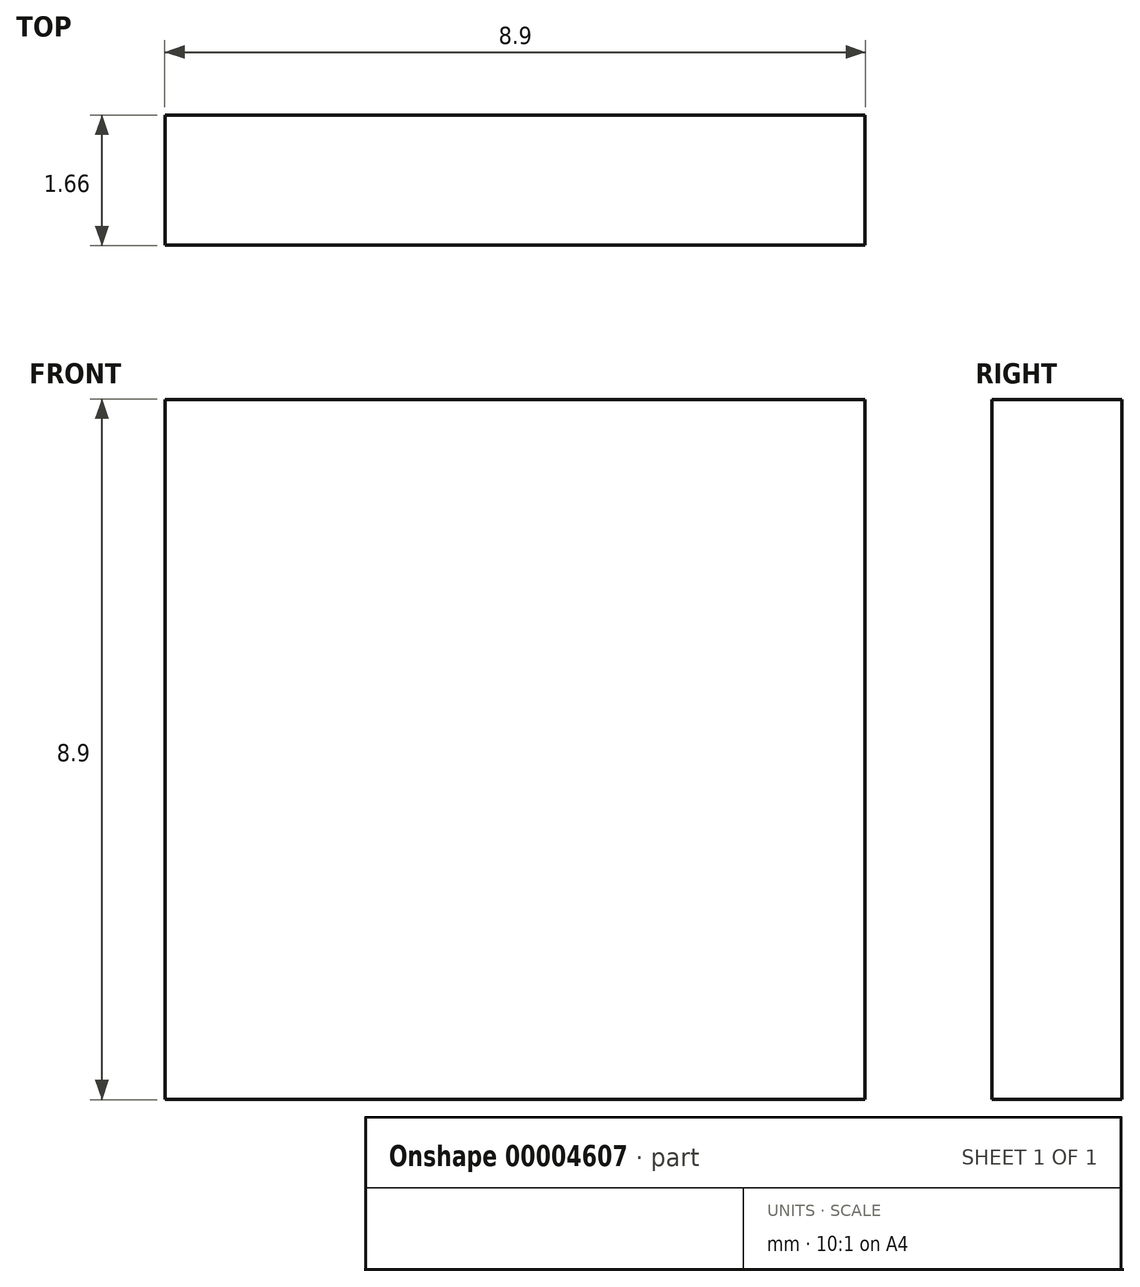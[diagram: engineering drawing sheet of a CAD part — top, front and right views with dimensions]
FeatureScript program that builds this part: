
annotation { "Feature Type Name" : "Feature", "Feature Type Description" : "" }
export const myFeature = defineFeature(function(context is Context, id is Id, definition is map)
    precondition{}
    {
        {
            var Q0;
            Q0=qCreatedBy(makeId("Right.planeOp"),FACE);
            var sketch = newSketch(context, id + "F0", { "sketchPlane" : qUnion([Q0])});
            skLineSegment(sketch, "E0.rect.bottom", {"start": v(0.83, -4.45) * mm, "end": v(-0.83, -4.45) * mm});
            skLineSegment(sketch, "E0.rect.top", {"start": v(0.83, 4.44) * mm, "end": v(-0.83, 4.44) * mm});
            skLineSegment(sketch, "E0.rect.left", {"start": v(0.83, -4.45) * mm, "end": v(0.83, 4.44) * mm});
            skLineSegment(sketch, "E0.rect.right", {"start": v(-0.83, -4.45) * mm, "end": v(-0.83, 4.44) * mm});
            skPoint(sketch, "E0.rect.middle", {"position": v(0, 0) * mm});
            skSolve(sketch);
        }
        {
            var Q0;
            Q0=makeQuery(id+"F0.imprint","IMPRINT",FACE,{"disambiguationData":[TD([[makeQuery(id+"F0.imprint","IMPRINT",EDGE,{"derivedFrom":sQuery(id+"F0.wireOp",EDGE,"E0.rect.bottom")}),-1.0]])]});
            extrude(context, id + "F1", {"entities" : qUnion([Q0]), "endBound" : BoundingType.SYMMETRIC, "depth" : 8.9 * mm});
        }
    });
